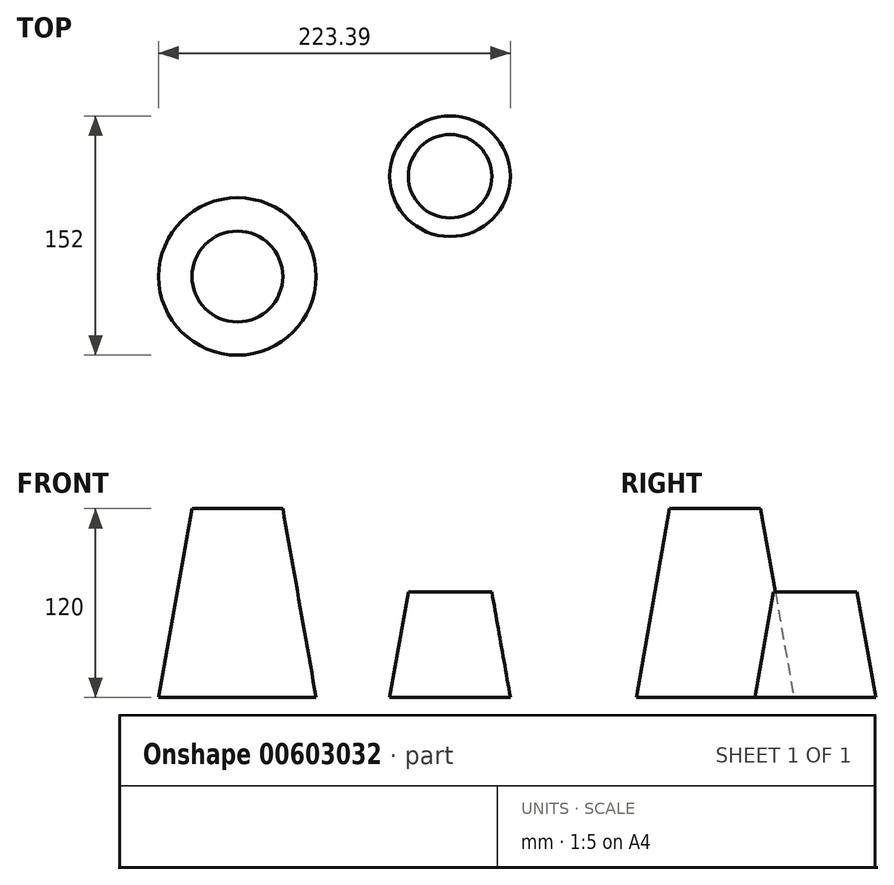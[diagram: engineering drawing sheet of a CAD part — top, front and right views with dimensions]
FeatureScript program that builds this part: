
annotation { "Feature Type Name" : "Feature", "Feature Type Description" : "" }
export const myFeature = defineFeature(function(context is Context, id is Id, definition is map)
    precondition{}
    {
        {
            var Q0;
            Q0=qCreatedBy(makeId("Top.planeOp"),FACE);
            var sketch = newSketch(context, id + "F0", { "sketchPlane" : qUnion([Q0])});
            skCircle(sketch, "E0", {"center": v(0, 0) * mm, "radius": 38.5 * mm});
            skSolve(sketch);
        }
        {
            var Q0;
            Q0=makeQuery(id+"F0.imprint","IMPRINT",FACE,{"disambiguationData":[TD([[makeQuery(id+"F0.imprint","IMPRINT",EDGE,{"derivedFrom":sQuery(id+"F0.wireOp",EDGE,"E0")}),1.0]])]});
            extrude(context, id + "F1", {"entities" : qUnion([Q0]), "depth" : 67 * mm, "offsetDistance" : 25 * mm});
        }
        {
            var Q0;
            Q0=makeQuery(id+"F1.opExtrude","CAP_EDGE",EDGE,{"disambiguationData":[OSD([sQuery(id+"F0.wireOp",EDGE,"E0")])],"isStart":false});
            chamfer(context, id + "F2", {"entities" : qUnion([Q0]), "chamferType" : ChamferType.OFFSET_ANGLE, "width" : 12 * mm, "oppositeDirection" : false, "angle" : 80 * degree, "tangentPropagation" : true});
        }
        {
            var Q0;
            Q0=qCreatedBy(makeId("Top.planeOp"),FACE);
            var sketch = newSketch(context, id + "F3", { "sketchPlane" : qUnion([Q0])});
            skCircle(sketch, "E1", {"center": v(-135.07, -63.68) * mm, "radius": 50 * mm});
            skSolve(sketch);
        }
        {
            var Q0;
            Q0=makeQuery(id+"F3.imprint","IMPRINT",FACE,{"disambiguationData":[TD([[makeQuery(id+"F3.imprint","IMPRINT",EDGE,{"derivedFrom":sQuery(id+"F3.wireOp",EDGE,"E1")}),1.0]])]});
            extrude(context, id + "F4", {"entities" : qUnion([Q0]), "depth" : 120 * mm, "offsetDistance" : 25 * mm, "hasDraft" : true, "draftAngle" : 10 * degree, "draftPullDirection" : true});
        }
    });
